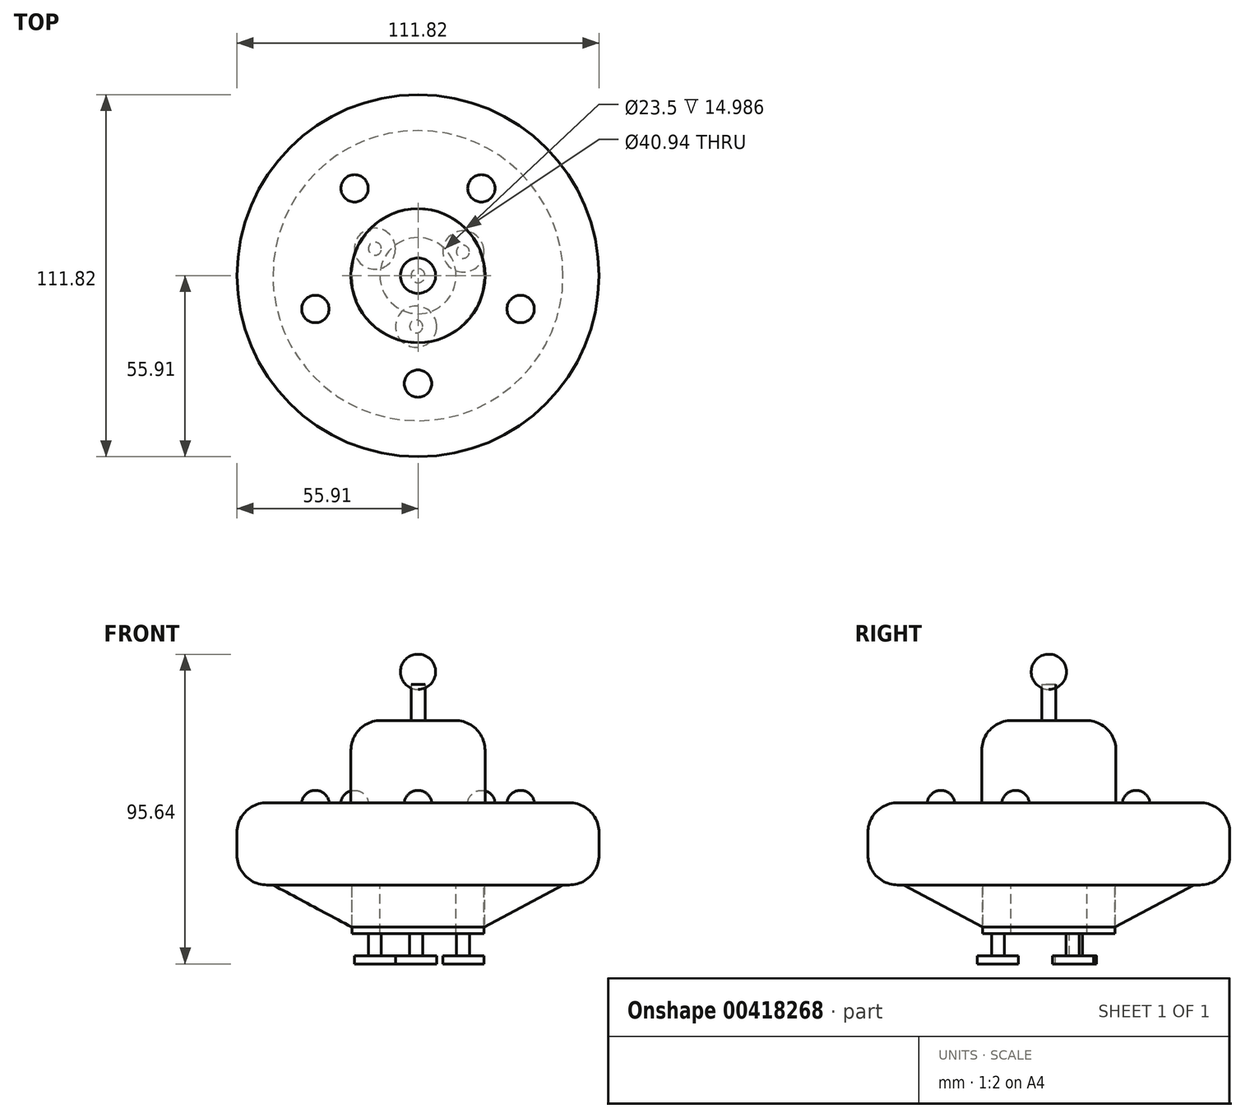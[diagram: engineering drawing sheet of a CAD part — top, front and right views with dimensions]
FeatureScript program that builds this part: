
annotation { "Feature Type Name" : "Feature", "Feature Type Description" : "" }
export const myFeature = defineFeature(function(context is Context, id is Id, definition is map)
    precondition{}
    {
        {
            var Q0;
            Q0=qCreatedBy(makeId("Top.planeOp"),FACE);
            var sketch = newSketch(context, id + "F0", { "sketchPlane" : qUnion([Q0])});
            skCircle(sketch, "E0", {"center": v(0, 0) * mm, "radius": 55.9 * mm});
            skCircle(sketch, "E1", {"center": v(0, 0) * mm, "radius": 20.7 * mm});
            skSolve(sketch);
        }
        {
            var Q0;
            Q0=makeQuery(id+"F0.imprint","IMPRINT",FACE,{"disambiguationData":[TD([[makeQuery(id+"F0.imprint","IMPRINT",EDGE,{"derivedFrom":sQuery(id+"F0.wireOp",EDGE,"E0")}),1.0]])]});
            extrude(context, id + "F1", {"entities" : qUnion([Q0]), "depth" : 25.4 * mm});
        }
        {
            var Q0;
            Q0=makeQuery(id+"F0.imprint","IMPRINT",FACE,{"disambiguationData":[TD([[makeQuery(id+"F0.imprint","IMPRINT",EDGE,{"derivedFrom":sQuery(id+"F0.wireOp",EDGE,"E1")}),1.0]])]});
            extrude(context, id + "F2", {"entities" : qUnion([Q0]), "operationType" : NewBodyOperationType.ADD, "depth" : 50.8 * mm});
        }
        {
            var Q0;
            Q0=makeQuery(id+"F1.opExtrude","CAP_EDGE",EDGE,{"disambiguationData":[OSD([sQuery(id+"F0.wireOp",EDGE,"E0")])],"isStart":false});
            var Q1;
            Q1=makeQuery(id+"F1.opExtrude","CAP_EDGE",EDGE,{"disambiguationData":[OSD([sQuery(id+"F0.wireOp",EDGE,"E0")])],"isStart":true});
            var Q2;
            Q2=makeQuery(id+"F2.opExtrude","CAP_EDGE",EDGE,{"disambiguationData":[OSD([sQuery(id+"F0.wireOp",EDGE,"E1")])],"isStart":false});
            fillet(context, id + "F3", {"entities" : qUnion([Q0, Q1, Q2]), "radius" : 9.2 * mm, "tangentPropagation" : true, "allowEdgeOverflow" : false});
        }
        {
            var Q0;
            Q0=qCreatedBy(makeId("Top.planeOp"),FACE);
            var sketch = newSketch(context, id + "F4", { "sketchPlane" : qUnion([Q0])});
            skCircle(sketch, "E2", {"center": v(0, 0) * mm, "radius": 20.42 * mm});
            skCircle(sketch, "E3", {"center": v(0, 0) * mm, "radius": 11.75 * mm});
            skLineSegment(sketch, "E4", {"start": v(3.34, -20.42) * mm, "end": v(0, -20.42) * mm});
            skPoint(sketch, "E5.end.orphan", {"position": v(0, 74.46) * mm});
            skPoint(sketch, "E6.start.orphan", {"position": v(-44.43, 0) * mm});
            skPoint(sketch, "E7.end.orphan", {"position": v(0, -44.5) * mm});
            skPoint(sketch, "E7.start.orphan", {"position": v(43.38, 0) * mm});
            skSolve(sketch);
        }
        {
            var Q0;
            Q0=makeQuery(id+"F4.imprint","IMPRINT",FACE,{"disambiguationData":[TD([[makeQuery(id+"F4.imprint","IMPRINT",EDGE,{"derivedFrom":sQuery(id+"F4.wireOp",EDGE,"E2")}),1.0]])]});
            extrude(context, id + "F5", {"entities" : qUnion([Q0]), "operationType" : NewBodyOperationType.ADD, "oppositeDirection" : true, "depth" : 15 * mm});
        }
        {
            var Q0;
            Q0=qCreatedBy(makeId("Top.planeOp"),FACE);
            cPlane(context, id + "F6", {"entities" : qUnion([Q0]), "cplaneType" : CPlaneType.OFFSET, "offset" : 50.8 * mm, "width" : 152.4 * mm, "height" : 152.4 * mm});
        }
        {
            var Q0;
            Q0=qCreatedBy(id+"F6.planeOp",FACE);
            var sketch = newSketch(context, id + "F7", { "sketchPlane" : qUnion([Q0])});
            skCircle(sketch, "E8", {"center": v(0, 0) * mm, "radius": 2.16 * mm});
            skSolve(sketch);
        }
        {
            var Q0;
            Q0 = qSketchRegion(id + "F7", true);
            extrude(context, id + "F8", {"entities" : qUnion([Q0]), "operationType" : NewBodyOperationType.ADD, "depth" : 11.18 * mm});
        }
        {
            var Q0;
            Q0=qCreatedBy(makeId("Front.planeOp"),FACE);
            var sketch = newSketch(context, id + "F9", { "sketchPlane" : qUnion([Q0])});
            skCircle(sketch, "E9", {"center": v(0, 65.82) * mm, "radius": 5.44 * mm});
            skLineSegment(sketch, "E10", {"start": v(0, 71.26) * mm, "end": v(0, 60.38) * mm});
            skSolve(sketch);
        }
        {
            var Q0;
            {var subQ0=sQuery(id+"F9.wireOp",EDGE,"E10");Q0=makeQuery(id+"F9.imprint","IMPRINT",FACE,{"disambiguationData":[TD([[makeQuery(id+"F9.imprint","IMPRINT",EDGE,{"derivedFrom":subQ0}),-1.0]])]});}
            var Q1;
            Q1=sQuery(id+"F9.wireOp",EDGE,"E10");
            revolve(context, id + "F10", {"entities" : qUnion([Q0]), "axis" : qUnion([Q1]), "revolveType" : RevolveType.FULL, "oppositeDirection" : true});
        }
        {
            var Q0;
            Q0=qCreatedBy(makeId("Front.planeOp"),FACE);
            var sketch = newSketch(context, id + "F11", { "sketchPlane" : qUnion([Q0])});
            skPoint(sketch, "E11.end.orphan", {"position": v(17.05, 0) * mm});
            skLineSegment(sketch, "E12", {"start": v(20.47, -13.02) * mm, "end": v(44.81, 0) * mm});
            skLineSegment(sketch, "E13", {"start": v(44.81, 0) * mm, "end": v(20.47, 0) * mm});
            skLineSegment(sketch, "E14", {"start": v(20.47, 0) * mm, "end": v(20.47, -13.02) * mm});
            skSolve(sketch);
        }
        {
            var Q0;
            Q0 = qSketchRegion(id + "F11", true);
            var Q1;
            {var subQ0=sQuery(id+"F0.wireOp",EDGE,"E1");var subQ1=sQuery(id+"F0.wireOp",EDGE,"E0");Q1=makeQuery(id+"F3.opFillet","BLEND_EDGE",EDGE,{"blendedFrom":[makeQuery(id+"F1.opExtrude","CAP_EDGE",EDGE,{"disambiguationData":[OSD([subQ1])],"isStart":true}),makeQuery(id+"F2.boolean.opBoolean","MERGE",FACE,{"derivedFrom":[makeQuery(id+"F1.opExtrude","CAP_FACE",FACE,{"disambiguationData":[OSD([subQ1,subQ0])],"isStart":true}),makeQuery(id+"F2.opExtrude","CAP_FACE",FACE,{"disambiguationData":[OSD([subQ0])],"isStart":true})]})],"blendedInto":[makeQuery(id+"F2.boolean.opBoolean","MERGE",FACE,{"derivedFrom":[makeQuery(id+"F1.opExtrude","CAP_FACE",FACE,{"disambiguationData":[OSD([subQ1,subQ0])],"isStart":true}),makeQuery(id+"F2.opExtrude","CAP_FACE",FACE,{"disambiguationData":[OSD([subQ0])],"isStart":true})]})]});}
            revolve(context, id + "F12", {"entities" : qUnion([Q0]), "axis" : qUnion([Q1]), "revolveType" : RevolveType.FULL});
        }
        {
            var Q0;
            Q0=makeQuery(id+"F5.opExtrude","CAP_FACE",FACE,{"disambiguationData":[OSD([sQuery(id+"F4.wireOp",EDGE,"E2"),sQuery(id+"F4.wireOp",EDGE,"E3")])],"isStart":false});
            var sketch = newSketch(context, id + "F13", { "sketchPlane" : qUnion([Q0])});
            skCircle(sketch, "E15", {"center": v(-13.31, -8.32) * mm, "radius": 2.01 * mm});
            skCircle(sketch, "E16.1.0", {"center": v(-0.55, 15.7) * mm, "radius": 2.01 * mm});
            skCircle(sketch, "E16.2.0", {"center": v(13.86, -7.37) * mm, "radius": 2.01 * mm});
            skPoint(sketch, "E16.center", {"position": v(0, 0) * mm});
            skLineSegment(sketch, "E16.anchor1", {"start": v(0, 0) * mm, "end": v(-13.31, -8.32) * mm, "construction": true});
            skLineSegment(sketch, "E16.anchor2", {"start": v(0, 0) * mm, "end": v(13.86, -7.37) * mm, "construction": true});
            skSolve(sketch);
        }
        {
            var Q0;
            Q0 = qSketchRegion(id + "F13", true);
            extrude(context, id + "F14", {"entities" : qUnion([Q0]), "depth" : 6.86 * mm});
        }
        {
            var Q0;
            Q0=makeQuery(id+"F14.opExtrude","CAP_FACE",FACE,{"disambiguationData":[OSD([sQuery(id+"F13.wireOp",EDGE,"E15")])],"isStart":false});
            var sketch = newSketch(context, id + "F15", { "sketchPlane" : qUnion([Q0])});
            skCircle(sketch, "E17", {"center": v(-13.31, -8.32) * mm, "radius": 6.35 * mm});
            skCircle(sketch, "E18", {"center": v(14, -7.46) * mm, "radius": 6.35 * mm});
            skCircle(sketch, "E19", {"center": v(-0.6, 15.72) * mm, "radius": 6.35 * mm});
            skSolve(sketch);
        }
        {
            var Q0;
            Q0=makeQuery(id+"F15.imprint","IMPRINT",FACE,{"disambiguationData":[TD([[makeQuery(id+"F15.imprint","IMPRINT",EDGE,{"derivedFrom":sQuery(id+"F15.wireOp",EDGE,"E17")}),1.0]])]});
            var Q1;
            Q1=makeQuery(id+"F15.imprint","IMPRINT",FACE,{"disambiguationData":[TD([[makeQuery(id+"F15.imprint","IMPRINT",EDGE,{"derivedFrom":sQuery(id+"F15.wireOp",EDGE,"E18")}),1.0]])]});
            var Q2;
            Q2=makeQuery(id+"F15.imprint","IMPRINT",FACE,{"disambiguationData":[TD([[makeQuery(id+"F15.imprint","IMPRINT",EDGE,{"derivedFrom":sQuery(id+"F15.wireOp",EDGE,"E19")}),1.0]])]});
            var Q3;
            Q3=makeQuery(id+"F15.imprint","IMPRINT",FACE,{"disambiguationData":[TD([[makeQuery(id+"F15.imprint","IMPRINT",EDGE,{"derivedFrom":makeQuery(id+"F14.opExtrude","CAP_EDGE",EDGE,{"disambiguationData":[OSD([sQuery(id+"F13.wireOp",EDGE,"E15")])],"isStart":false})}),1.0]])]});
            extrude(context, id + "F16", {"entities" : qUnion([Q0, Q1, Q2, Q3]), "depth" : 2.54 * mm});
        }
        {
            var Q0;
            Q0=makeQuery(id+"F1.opExtrude","CAP_FACE",FACE,{"disambiguationData":[OSD([sQuery(id+"F0.wireOp",EDGE,"E0"),sQuery(id+"F0.wireOp",EDGE,"E1")])],"isStart":false});
            var sketch = newSketch(context, id + "F17", { "sketchPlane" : qUnion([Q0])});
            skCircle(sketch, "E20", {"center": v(0, -33.33) * mm, "radius": 4.23 * mm});
            skCircle(sketch, "E21.1.0", {"center": v(31.7, -10.3) * mm, "radius": 4.23 * mm});
            skCircle(sketch, "E21.2.0", {"center": v(19.6, 26.96) * mm, "radius": 4.23 * mm});
            skPoint(sketch, "E21.center", {"position": v(0, 0) * mm});
            skCircle(sketch, "E22.1.3.0", {"center": v(-19.6, 26.96) * mm, "radius": 4.23 * mm});
            skCircle(sketch, "E22.1.4.0", {"center": v(-31.7, -10.3) * mm, "radius": 4.23 * mm});
            skSolve(sketch);
        }
        {
            var Q0;
            Q0 = qSketchRegion(id + "F17", true);
            extrude(context, id + "F18", {"entities" : qUnion([Q0]), "depth" : 3.8 * mm});
        }
        {
            var Q0;
            Q0=makeQuery(id+"F18.opExtrude","CAP_EDGE",EDGE,{"disambiguationData":[OSD([sQuery(id+"F17.wireOp",EDGE,"E22.1.4.0")])],"isStart":false});
            var Q1;
            Q1=makeQuery(id+"F18.opExtrude","CAP_EDGE",EDGE,{"disambiguationData":[OSD([sQuery(id+"F17.wireOp",EDGE,"E20")])],"isStart":false});
            var Q2;
            Q2=makeQuery(id+"F18.opExtrude","CAP_EDGE",EDGE,{"disambiguationData":[OSD([sQuery(id+"F17.wireOp",EDGE,"E21.1.0")])],"isStart":false});
            var Q3;
            Q3=makeQuery(id+"F18.opExtrude","CAP_EDGE",EDGE,{"disambiguationData":[OSD([sQuery(id+"F17.wireOp",EDGE,"E22.1.3.0")])],"isStart":false});
            var Q4;
            Q4=makeQuery(id+"F18.opExtrude","CAP_EDGE",EDGE,{"disambiguationData":[OSD([sQuery(id+"F17.wireOp",EDGE,"E21.2.0")])],"isStart":false});
            fillet(context, id + "F19", {"entities" : qUnion([Q0, Q1, Q2, Q3, Q4]), "radius" : 4.22 * mm, "tangentPropagation" : true, "allowEdgeOverflow" : false});
        }
    });
